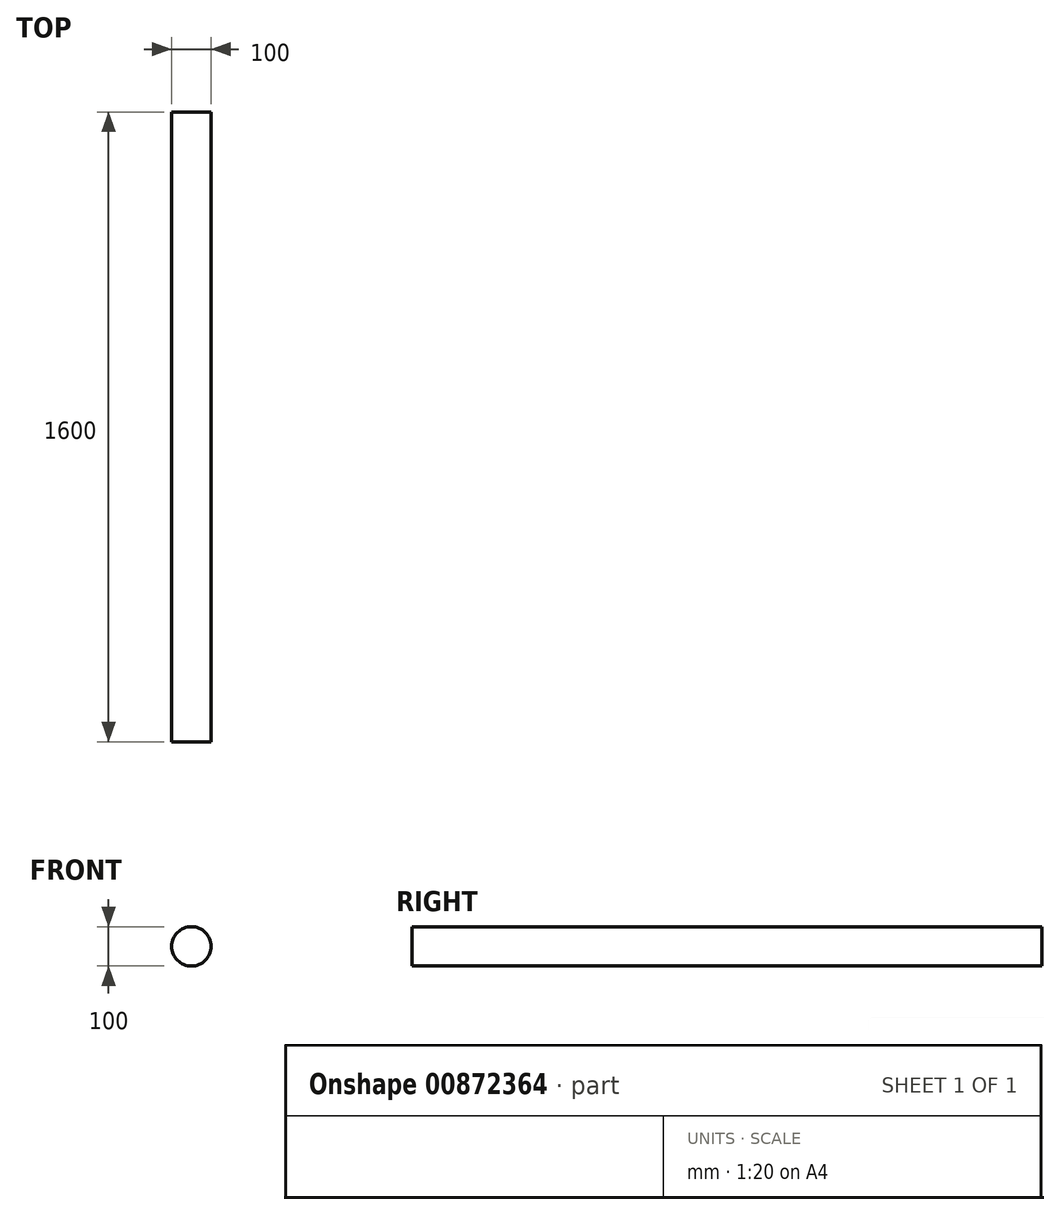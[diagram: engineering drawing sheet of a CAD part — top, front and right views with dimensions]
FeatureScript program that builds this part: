
annotation { "Feature Type Name" : "Feature", "Feature Type Description" : "" }
export const myFeature = defineFeature(function(context is Context, id is Id, definition is map)
    precondition{}
    {
        {
            var Q0;
            Q0=qCreatedBy(makeId("Front.planeOp"),FACE);
            var sketch = newSketch(context, id + "F0", { "sketchPlane" : qUnion([Q0])});
            skCircle(sketch, "E0", {"center": v(-47.73, 27.46) * mm, "radius": 50 * mm});
            skSolve(sketch);
        }
        {
            var Q0;
            Q0=makeQuery(id+"F0.imprint","IMPRINT",FACE,{"disambiguationData":[TD([[makeQuery(id+"F0.imprint","IMPRINT",EDGE,{"derivedFrom":sQuery(id+"F0.wireOp",EDGE,"E0")}),1.0]])]});
            extrude(context, id + "F1", {"entities" : qUnion([Q0]), "depth" : 1600 * mm, "offsetDistance" : 25 * mm});
        }
    });
